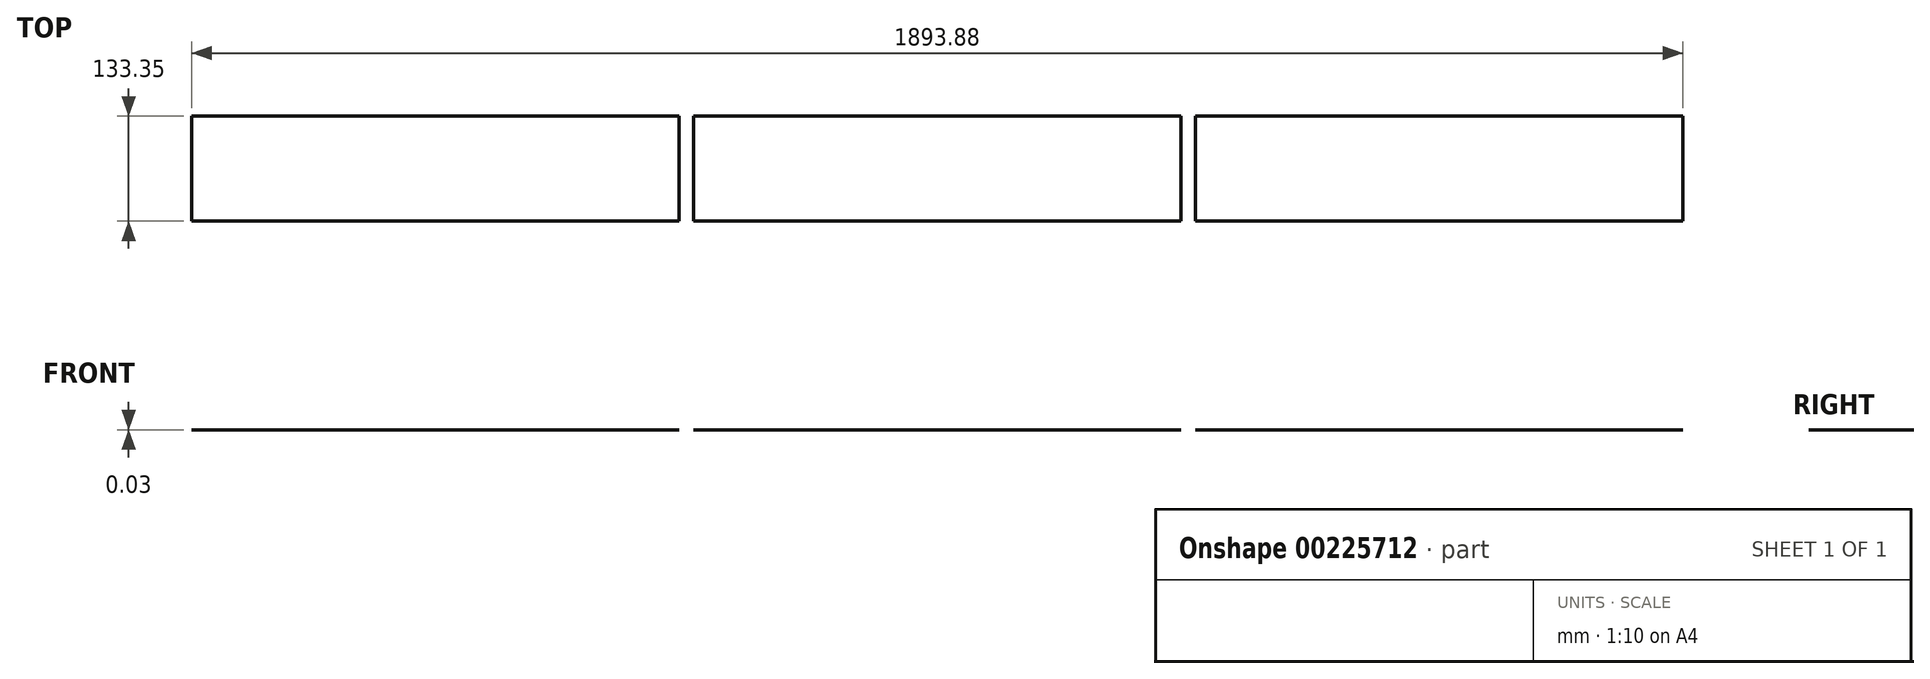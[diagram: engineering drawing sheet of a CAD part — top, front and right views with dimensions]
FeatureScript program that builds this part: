
annotation { "Feature Type Name" : "Feature", "Feature Type Description" : "" }
export const myFeature = defineFeature(function(context is Context, id is Id, definition is map)
    precondition{}
    {
        {
            var Q0;
            Q0=qCreatedBy(makeId("Top.planeOp"),FACE);
            var sketch = newSketch(context, id + "F0", { "sketchPlane" : qUnion([Q0])});
            skLineSegment(sketch, "E0.bottom", {"start": v(-662.7, -202.05) * mm, "end": v(1267.7, -202.05) * mm});
            skLineSegment(sketch, "E0.top", {"start": v(-662.7, -335.4) * mm, "end": v(1267.7, -335.4) * mm});
            skLineSegment(sketch, "E0.left", {"start": v(-662.7, -202.05) * mm, "end": v(-662.7, -335.4) * mm});
            skLineSegment(sketch, "E0.right", {"start": v(1267.7, -202.05) * mm, "end": v(1267.7, -335.4) * mm});
            skSolve(sketch);
        }
        {
            var Q0;
            Q0=qSketchRegion(id+"F0",true);
            extrude(context, id + "F1", {"entities" : qUnion([Q0]), "oppositeDirection" : true, "depth" : 23 / 812.8 * mm});
        }
        {
            var Q0;
            Q0=makeQuery(id+"F1.opExtrude","SWEPT_FACE",FACE,{"disambiguationData":[OSD([sQuery(id+"F0.wireOp",EDGE,"E0.top")])]});
            var sketch = newSketch(context, id + "F2", { "sketchPlane" : qUnion([Q0])});
            skLineSegment(sketch, "E1.bottom", {"start": v(-662.7, 0) * mm, "end": v(-644.45, 0) * mm});
            skLineSegment(sketch, "E1.top", {"start": v(-662.7, -6.35) * mm, "end": v(-644.45, -6.35) * mm});
            skLineSegment(sketch, "E1.left", {"start": v(-662.7, 0) * mm, "end": v(-662.7, -6.35) * mm});
            skLineSegment(sketch, "E1.right", {"start": v(-644.45, 0) * mm, "end": v(-644.45, -6.35) * mm});
            skSolve(sketch);
        }
        {
            var Q0;
            Q0=makeQuery(id+"F2.imprint","IMPRINT",FACE,{"disambiguationData":[TD([[makeQuery(id+"F2.imprint","IMPRINT",EDGE,{"derivedFrom":sQuery(id+"F2.wireOp",EDGE,"E1.bottom")}),-1.0]])]});
            extrude(context, id + "F3", {"entities" : qUnion([Q0]), "operationType" : NewBodyOperationType.REMOVE, "endBound" : BoundingType.THROUGH_ALL, "oppositeDirection" : true, "depth" : 25.4 * mm});
        }
        {
            var Q0;
            Q0=makeQuery(id+"F1.opExtrude","SWEPT_FACE",FACE,{"disambiguationData":[OSD([sQuery(id+"F0.wireOp",EDGE,"E0.top")])]});
            var sketch = newSketch(context, id + "F4", { "sketchPlane" : qUnion([Q0])});
            skLineSegment(sketch, "E2.bottom", {"start": v(1267.7, 0) * mm, "end": v(1249.43, 0) * mm});
            skLineSegment(sketch, "E2.top", {"start": v(1267.7, -6.35) * mm, "end": v(1249.43, -6.35) * mm});
            skLineSegment(sketch, "E2.left", {"start": v(1267.7, 0) * mm, "end": v(1267.7, -6.35) * mm});
            skLineSegment(sketch, "E2.right", {"start": v(1249.43, 0) * mm, "end": v(1249.43, -6.35) * mm});
            skSolve(sketch);
        }
        {
            var Q0;
            Q0=makeQuery(id+"F4.imprint","IMPRINT",FACE,{"disambiguationData":[TD([[makeQuery(id+"F4.imprint","IMPRINT",EDGE,{"derivedFrom":sQuery(id+"F4.wireOp",EDGE,"E2.bottom")}),-1.0]])]});
            extrude(context, id + "F5", {"entities" : qUnion([Q0]), "operationType" : NewBodyOperationType.REMOVE, "endBound" : BoundingType.THROUGH_ALL, "oppositeDirection" : true, "depth" : 25.4 * mm});
        }
        {
            var Q0;
            Q0=makeQuery(id+"F1.opExtrude","SWEPT_FACE",FACE,{"disambiguationData":[OSD([sQuery(id+"F0.wireOp",EDGE,"E0.top")])]});
            var sketch = newSketch(context, id + "F6", { "sketchPlane" : qUnion([Q0])});
            skLineSegment(sketch, "E3.bottom", {"start": v(612.05, 0) * mm, "end": v(630.3, 0) * mm});
            skLineSegment(sketch, "E3.top", {"start": v(612.05, -6.35) * mm, "end": v(630.3, -6.35) * mm});
            skLineSegment(sketch, "E3.left", {"start": v(612.05, 0) * mm, "end": v(612.05, -6.35) * mm});
            skLineSegment(sketch, "E3.right", {"start": v(630.3, 0) * mm, "end": v(630.3, -6.35) * mm});
            skSolve(sketch);
        }
        {
            var Q0;
            Q0=makeQuery(id+"F6.imprint","IMPRINT",FACE,{"disambiguationData":[TD([[makeQuery(id+"F6.imprint","IMPRINT",EDGE,{"derivedFrom":sQuery(id+"F6.wireOp",EDGE,"E3.bottom")}),-1.0]])]});
            extrude(context, id + "F7", {"entities" : qUnion([Q0]), "operationType" : NewBodyOperationType.REMOVE, "endBound" : BoundingType.THROUGH_ALL, "oppositeDirection" : true, "depth" : 25.4 * mm});
        }
        {
            var Q0;
            Q0=makeQuery(id+"F1.opExtrude","SWEPT_FACE",FACE,{"disambiguationData":[OSD([sQuery(id+"F0.wireOp",EDGE,"E0.top")])]});
            var sketch = newSketch(context, id + "F8", { "sketchPlane" : qUnion([Q0])});
            skLineSegment(sketch, "E4.bottom", {"start": v(-25.33, 0) * mm, "end": v(-7.07, 0) * mm});
            skLineSegment(sketch, "E4.top", {"start": v(-25.33, -6.35) * mm, "end": v(-7.07, -6.35) * mm});
            skLineSegment(sketch, "E4.left", {"start": v(-25.33, 0) * mm, "end": v(-25.33, -6.35) * mm});
            skLineSegment(sketch, "E4.right", {"start": v(-7.07, 0) * mm, "end": v(-7.07, -6.35) * mm});
            skSolve(sketch);
        }
        {
            var Q0;
            Q0=makeQuery(id+"F8.imprint","IMPRINT",FACE,{"disambiguationData":[TD([[makeQuery(id+"F8.imprint","IMPRINT",EDGE,{"derivedFrom":sQuery(id+"F8.wireOp",EDGE,"E4.bottom")}),-1.0]])]});
            extrude(context, id + "F9", {"entities" : qUnion([Q0]), "operationType" : NewBodyOperationType.REMOVE, "endBound" : BoundingType.THROUGH_ALL, "oppositeDirection" : true, "depth" : 25.4 * mm});
        }
    });
